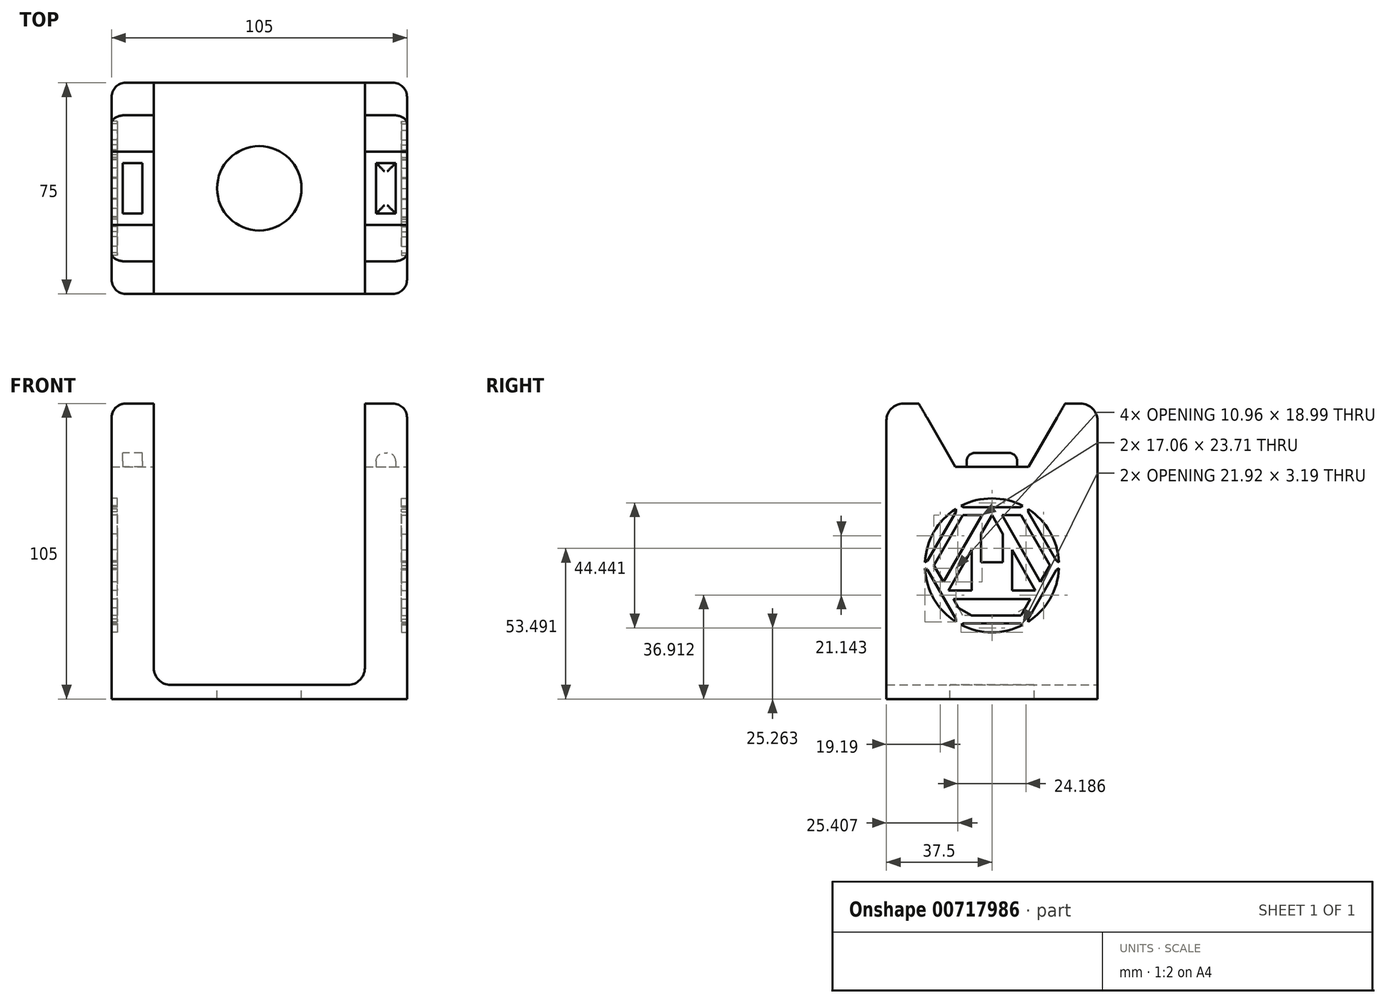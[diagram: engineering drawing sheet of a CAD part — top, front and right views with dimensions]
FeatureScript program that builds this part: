
annotation { "Feature Type Name" : "Feature", "Feature Type Description" : "" }
export const myFeature = defineFeature(function(context is Context, id is Id, definition is map)
    precondition{}
    {
        {
            var Q0;
            Q0=qCreatedBy(makeId("Front.planeOp"),FACE);
            var sketch = newSketch(context, id + "F0", { "sketchPlane" : qUnion([Q0])});
            skLineSegment(sketch, "E0.bottom", {"start": v(52.5, -2.5) * mm, "end": v(-52.5, -2.5) * mm});
            skLineSegment(sketch, "E0.top", {"start": v(52.5, 2.5) * mm, "end": v(-52.5, 2.5) * mm});
            skLineSegment(sketch, "E0.left", {"start": v(52.5, -2.5) * mm, "end": v(52.5, 2.5) * mm});
            skLineSegment(sketch, "E0.right", {"start": v(-52.5, -2.5) * mm, "end": v(-52.5, 2.5) * mm});
            skPoint(sketch, "E0.middle", {"position": v(0, 0) * mm});
            skLineSegment(sketch, "E1.bottom", {"start": v(-52.5, 2.5) * mm, "end": v(-37.5, 2.5) * mm});
            skLineSegment(sketch, "E1.top", {"start": v(-52.5, 102.5) * mm, "end": v(-37.5, 102.5) * mm});
            skLineSegment(sketch, "E1.left", {"start": v(-52.5, 2.5) * mm, "end": v(-52.5, 102.5) * mm});
            skLineSegment(sketch, "E1.right", {"start": v(-37.5, 2.5) * mm, "end": v(-37.5, 102.5) * mm});
            skLineSegment(sketch, "E2.bottom", {"start": v(52.5, 2.5) * mm, "end": v(37.5, 2.5) * mm});
            skLineSegment(sketch, "E2.top", {"start": v(52.5, 102.5) * mm, "end": v(37.5, 102.5) * mm});
            skLineSegment(sketch, "E2.left", {"start": v(52.5, 2.5) * mm, "end": v(52.5, 102.5) * mm});
            skLineSegment(sketch, "E2.right", {"start": v(37.5, 2.5) * mm, "end": v(37.5, 102.5) * mm});
            skLineSegment(sketch, "E3", {"start": v(-37.5, 2.5) * mm, "end": v(0, 2.5) * mm});
            skLineSegment(sketch, "E4", {"start": v(-37.5, 2.5) * mm, "end": v(-37.5, 40) * mm});
            skLineSegment(sketch, "E5", {"start": v(37.5, 40) * mm, "end": v(37.5, 2.5) * mm});
            skSolve(sketch);
        }
        {
            var Q0;
            Q0 = qSketchRegion(id + "F0", true);
            extrude(context, id + "F1", {"entities" : qUnion([Q0]), "depth" : 75 * mm, "offsetDistance" : 25 * mm});
        }
        {
            var Q0;
            Q0=makeQuery(id+"F1.opExtrude","SWEPT_FACE",FACE,{"disambiguationData":[OSD([sQuery(id+"F0.wireOp",EDGE,"E0.left"),sQuery(id+"F0.wireOp",EDGE,"E2.left")])]});
            var sketch = newSketch(context, id + "F2", { "sketchPlane" : qUnion([Q0])});
            skCircle(sketch, "E6.cCircle", {"center": v(-37.5, 102.5) * mm, "radius": 26 * mm, "construction": true});
            skLineSegment(sketch, "E6.0", {"start": v(-11.5, 102.5) * mm, "end": v(-24.5, 79.98) * mm});
            skLineSegment(sketch, "E6.1", {"start": v(-24.5, 79.98) * mm, "end": v(-50.5, 79.98) * mm});
            skLineSegment(sketch, "E6.2", {"start": v(-50.5, 79.98) * mm, "end": v(-63.5, 102.5) * mm});
            skLineSegment(sketch, "E6.3", {"start": v(-63.5, 102.5) * mm, "end": v(-50.5, 125.02) * mm});
            skLineSegment(sketch, "E6.4", {"start": v(-50.5, 125.02) * mm, "end": v(-24.5, 125.02) * mm});
            skLineSegment(sketch, "E6.5", {"start": v(-24.5, 125.02) * mm, "end": v(-11.5, 102.5) * mm});
            skSolve(sketch);
        }
        {
            var Q0;
            Q0 = qSketchRegion(id + "F2", true);
            extrude(context, id + "F3", {"entities" : qUnion([Q0]), "operationType" : NewBodyOperationType.REMOVE, "oppositeDirection" : true, "depth" : 122 * mm, "offsetDistance" : 25 * mm});
        }
        {
            var Q0;
            Q0=makeQuery(id+"F3.boolean.opBoolean","COPY",FACE,{"disambiguationData":[TD([makeQuery(id+"F1.opExtrude","SWEPT_FACE",FACE,{"disambiguationData":[OSD([sQuery(id+"F0.wireOp",EDGE,"E0.right"),sQuery(id+"F0.wireOp",EDGE,"E1.left")])]})])],"derivedFrom":makeQuery(id+"F3.opExtrude","SWEPT_FACE",FACE,{"disambiguationData":[OSD([sQuery(id+"F2.wireOp",EDGE,"E6.1")])]})});
            var sketch = newSketch(context, id + "F4", { "sketchPlane" : qUnion([Q0])});
            skLineSegment(sketch, "E7.bottom", {"start": v(-41.5, -50.5) * mm, "end": v(-48.5, -50.5) * mm});
            skLineSegment(sketch, "E7.top", {"start": v(-41.5, -24.5) * mm, "end": v(-48.5, -24.5) * mm});
            skLineSegment(sketch, "E7.left", {"start": v(-41.5, -50.5) * mm, "end": v(-41.5, -24.5) * mm});
            skLineSegment(sketch, "E7.right", {"start": v(-48.5, -50.5) * mm, "end": v(-48.5, -24.5) * mm});
            skPoint(sketch, "E7.middle", {"position": v(-45, -37.5) * mm});
            skPoint(sketch, "E7.middle.positionSnap0", {"position": v(-45, -24.5) * mm});
            skPoint(sketch, "E7.middle.positionSnap1", {"position": v(-37.5, -37.5) * mm});
            skPoint(sketch, "E7.centerSnap0", {"position": v(-45, -24.5) * mm});
            skPoint(sketch, "E7.centerSnap1", {"position": v(-37.5, -37.5) * mm});
            skLineSegment(sketch, "E8", {"start": v(0, 0) * mm, "end": v(0, -8.57) * mm});
            skLineSegment(sketch, "E9.MirrorCS", {"start": v(41.5, -50.5) * mm, "end": v(41.5, -24.5) * mm});
            skLineSegment(sketch, "E10.MirrorCS", {"start": v(48.5, -50.5) * mm, "end": v(48.5, -24.5) * mm});
            skLineSegment(sketch, "E11.MirrorCS", {"start": v(41.5, -24.5) * mm, "end": v(48.5, -24.5) * mm});
            skLineSegment(sketch, "E12.MirrorCS", {"start": v(41.5, -50.5) * mm, "end": v(48.5, -50.5) * mm});
            skLineSegment(sketch, "E13.bottom", {"start": v(-41.5, -46.5) * mm, "end": v(-48.5, -46.5) * mm});
            skLineSegment(sketch, "E13.top", {"start": v(-41.5, -28.5) * mm, "end": v(-48.5, -28.5) * mm});
            skLineSegment(sketch, "E13.left", {"start": v(-41.5, -46.5) * mm, "end": v(-41.5, -28.5) * mm});
            skLineSegment(sketch, "E13.right", {"start": v(-48.5, -46.5) * mm, "end": v(-48.5, -28.5) * mm});
            skLineSegment(sketch, "E14.MirrorCS", {"start": v(41.5, -28.5) * mm, "end": v(48.5, -28.5) * mm});
            skLineSegment(sketch, "E15.MirrorCS", {"start": v(41.5, -46.5) * mm, "end": v(48.5, -46.5) * mm});
            skSolve(sketch);
        }
        {
            var Q0;
            {var subQ0=sQuery(id+"F4.wireOp",EDGE,"E14.MirrorCS");Q0=makeQuery(id+"F4.imprint","IMPRINT",FACE,{"disambiguationData":[TD([[makeQuery(id+"F4.imprint","IMPRINT",EDGE,{"derivedFrom":subQ0}),-1.0]])]});}
            var Q1;
            Q1=makeQuery(id+"F4.imprint","IMPRINT",FACE,{"disambiguationData":[TD([[makeQuery(id+"F4.imprint","IMPRINT",EDGE,{"derivedFrom":sQuery(id+"F4.wireOp",EDGE,"E13.bottom")}),-1.0]])]});
            extrude(context, id + "F5", {"entities" : qUnion([Q0, Q1]), "operationType" : NewBodyOperationType.ADD, "depth" : 5 * mm, "offsetDistance" : 25 * mm});
        }
        {
            var Q0;
            Q0=makeQuery(id+"F5.opExtrude","CAP_EDGE",EDGE,{"disambiguationData":[OSD([sQuery(id+"F4.wireOp",EDGE,"E13.right")])],"isStart":false});
            var Q1;
            Q1=makeQuery(id+"F5.opExtrude","CAP_EDGE",EDGE,{"disambiguationData":[OSD([sQuery(id+"F4.wireOp",EDGE,"E13.top")])],"isStart":false});
            var Q2;
            Q2=makeQuery(id+"F5.opExtrude","CAP_EDGE",EDGE,{"disambiguationData":[OSD([sQuery(id+"F4.wireOp",EDGE,"E13.left")])],"isStart":false});
            var Q3;
            Q3=makeQuery(id+"F5.opExtrude","CAP_EDGE",EDGE,{"disambiguationData":[OSD([sQuery(id+"F4.wireOp",EDGE,"E13.bottom")])],"isStart":false});
            var Q4;
            Q4=makeQuery(id+"F5.opExtrude","CAP_EDGE",EDGE,{"disambiguationData":[OSD([sQuery(id+"F4.wireOp",EDGE,"E9.MirrorCS")])],"isStart":false});
            var Q5;
            Q5=makeQuery(id+"F5.opExtrude","CAP_EDGE",EDGE,{"disambiguationData":[OSD([sQuery(id+"F4.wireOp",EDGE,"E14.MirrorCS")])],"isStart":false});
            var Q6;
            Q6=makeQuery(id+"F5.opExtrude","CAP_EDGE",EDGE,{"disambiguationData":[OSD([sQuery(id+"F4.wireOp",EDGE,"E10.MirrorCS")])],"isStart":false});
            var Q7;
            Q7=makeQuery(id+"F5.opExtrude","CAP_EDGE",EDGE,{"disambiguationData":[OSD([sQuery(id+"F4.wireOp",EDGE,"E15.MirrorCS")])],"isStart":false});
            fillet(context, id + "F6", {"entities" : qUnion([Q0, Q1, Q2, Q3, Q4, Q5, Q6, Q7]), "radius" : 3 * mm, "tangentPropagation" : true, "allowEdgeOverflow" : false});
        }
        {
            var Q0;
            Q0=makeQuery(id+"F1.opExtrude","SWEPT_EDGE",EDGE,{"disambiguationData":[OSD([sQuery(id+"F0.wireOp",EDGE,"E1.bottom"),sQuery(id+"F0.wireOp",EDGE,"E3"),sQuery(id+"F0.wireOp",EDGE,"E4")])]});
            var Q1;
            Q1=makeQuery(id+"F1.opExtrude","SWEPT_EDGE",EDGE,{"disambiguationData":[OSD([sQuery(id+"F0.wireOp",EDGE,"E0.top"),sQuery(id+"F0.wireOp",EDGE,"E2.bottom"),sQuery(id+"F0.wireOp",EDGE,"E5")])]});
            var Q2;
            Q2=makeQuery(id+"F1.opExtrude","CAP_EDGE",EDGE,{"disambiguationData":[OSD([sQuery(id+"F0.wireOp",EDGE,"E1.top")])],"isStart":false});
            var Q3;
            Q3=makeQuery(id+"F1.opExtrude","CAP_EDGE",EDGE,{"disambiguationData":[OSD([sQuery(id+"F0.wireOp",EDGE,"E2.top")])],"isStart":false});
            var Q4;
            Q4=makeQuery(id+"F1.opExtrude","CAP_EDGE",EDGE,{"disambiguationData":[OSD([sQuery(id+"F0.wireOp",EDGE,"E2.top")])],"isStart":true});
            var Q5;
            Q5=makeQuery(id+"F1.opExtrude","CAP_EDGE",EDGE,{"disambiguationData":[OSD([sQuery(id+"F0.wireOp",EDGE,"E1.top")])],"isStart":true});
            fillet(context, id + "F7", {"entities" : qUnion([Q0, Q1, Q2, Q3, Q4, Q5]), "radius" : 6 * mm, "tangentPropagation" : true, "allowEdgeOverflow" : false});
        }
        {
            var Q0;
            Q0=makeQuery(id+"F1.opExtrude","CAP_EDGE",EDGE,{"disambiguationData":[OSD([sQuery(id+"F0.wireOp",EDGE,"E0.right"),sQuery(id+"F0.wireOp",EDGE,"E1.left")])],"isStart":false});
            var Q1;
            Q1=makeQuery(id+"F1.opExtrude","CAP_EDGE",EDGE,{"disambiguationData":[OSD([sQuery(id+"F0.wireOp",EDGE,"E0.right"),sQuery(id+"F0.wireOp",EDGE,"E1.left")])],"isStart":true});
            var Q2;
            Q2=makeQuery(id+"F1.opExtrude","CAP_EDGE",EDGE,{"disambiguationData":[OSD([sQuery(id+"F0.wireOp",EDGE,"E0.left"),sQuery(id+"F0.wireOp",EDGE,"E2.left")])],"isStart":false});
            var Q3;
            Q3=makeQuery(id+"F1.opExtrude","CAP_EDGE",EDGE,{"disambiguationData":[OSD([sQuery(id+"F0.wireOp",EDGE,"E0.left"),sQuery(id+"F0.wireOp",EDGE,"E2.left")])],"isStart":true});
            fillet(context, id + "F8", {"entities" : qUnion([Q0, Q1, Q2, Q3]), "radius" : 5 * mm, "tangentPropagation" : true, "allowEdgeOverflow" : false});
        }
        {
            var Q0;
            Q0=makeQuery(id+"F1.opExtrude","SWEPT_FACE",FACE,{"disambiguationData":[OSD([sQuery(id+"F0.wireOp",EDGE,"E0.left"),sQuery(id+"F0.wireOp",EDGE,"E2.left")])]});
            var sketch = newSketch(context, id + "F9", { "sketchPlane" : qUnion([Q0])});
            skCircle(sketch, "E16", {"center": v(-37.5, 44.98) * mm, "radius": 27.5 * mm});
            skLineSegment(sketch, "E17", {"start": v(-51.25, 68.8) * mm, "end": v(-65, 44.98) * mm});
            skLineSegment(sketch, "E18", {"start": v(-65, 44.98) * mm, "end": v(-51.25, 21.17) * mm});
            skLineSegment(sketch, "E19", {"start": v(-51.25, 21.17) * mm, "end": v(-23.75, 21.17) * mm});
            skLineSegment(sketch, "E20", {"start": v(-23.75, 21.17) * mm, "end": v(-10, 44.98) * mm});
            skLineSegment(sketch, "E21", {"start": v(-10, 44.98) * mm, "end": v(-23.75, 68.8) * mm});
            skLineSegment(sketch, "E22", {"start": v(-23.75, 68.8) * mm, "end": v(-51.25, 68.8) * mm});
            skCircle(sketch, "E23", {"center": v(-37.5, 44.98) * mm, "radius": 23.82 * mm});
            skLineSegment(sketch, "E24", {"start": v(-49.4, 65.6) * mm, "end": v(-61.32, 44.98) * mm});
            skLineSegment(sketch, "E25", {"start": v(-61.32, 44.98) * mm, "end": v(-49.4, 24.36) * mm});
            skLineSegment(sketch, "E26", {"start": v(-49.4, 24.36) * mm, "end": v(-25.6, 24.36) * mm});
            skLineSegment(sketch, "E27", {"start": v(-25.6, 24.36) * mm, "end": v(-13.68, 44.98) * mm});
            skLineSegment(sketch, "E28", {"start": v(-13.68, 44.98) * mm, "end": v(-25.6, 65.6) * mm});
            skLineSegment(sketch, "E29", {"start": v(-25.6, 65.6) * mm, "end": v(-49.4, 65.6) * mm});
            skLineSegment(sketch, "E30", {"start": v(-51.25, 27.55) * mm, "end": v(-51.25, 25.54) * mm});
            skLineSegment(sketch, "E31", {"start": v(-23.75, 27.55) * mm, "end": v(-23.75, 25.54) * mm});
            skLineSegment(sketch, "E32", {"start": v(-49.4, 24.36) * mm, "end": v(-51.25, 21.17) * mm});
            skLineSegment(sketch, "E33", {"start": v(-25.6, 24.36) * mm, "end": v(-23.75, 21.17) * mm});
            skLineSegment(sketch, "E34.MirrorCS", {"start": v(-45.72, 24.36) * mm, "end": v(-47.47, 23.35) * mm});
            skLineSegment(sketch, "E35.MirrorCS", {"start": v(-29.28, 24.36) * mm, "end": v(-27.53, 23.35) * mm});
            skLineSegment(sketch, "E36", {"start": v(-37.5, 44.98) * mm, "end": v(-37.6, 44.98) * mm});
            skLineSegment(sketch, "E37.MirrorCS", {"start": v(-51.25, 62.42) * mm, "end": v(-51.25, 64.43) * mm});
            skLineSegment(sketch, "E38.MirrorCS", {"start": v(-45.72, 65.6) * mm, "end": v(-47.47, 66.61) * mm});
            skLineSegment(sketch, "E39.MirrorCS", {"start": v(-29.28, 65.6) * mm, "end": v(-27.53, 66.61) * mm});
            skLineSegment(sketch, "E40.MirrorCS", {"start": v(-23.75, 62.42) * mm, "end": v(-23.75, 64.43) * mm});
            skLineSegment(sketch, "E41", {"start": v(-58.12, 33.08) * mm, "end": v(-55.36, 34.67) * mm});
            skLineSegment(sketch, "E42", {"start": v(-19.64, 34.67) * mm, "end": v(-16.87, 33.08) * mm});
            skLineSegment(sketch, "E43.MirrorCS", {"start": v(-59.47, 41.8) * mm, "end": v(-61.22, 42.8) * mm});
            skLineSegment(sketch, "E44.MirrorCS", {"start": v(-59.47, 48.17) * mm, "end": v(-61.22, 47.17) * mm});
            skLineSegment(sketch, "E45.MirrorCS", {"start": v(-15.53, 48.17) * mm, "end": v(-13.78, 47.17) * mm});
            skLineSegment(sketch, "E46.MirrorCS", {"start": v(-15.53, 41.8) * mm, "end": v(-13.78, 42.8) * mm});
            skCircle(sketch, "E47", {"center": v(-37.5, 44.98) * mm, "radius": 20.63 * mm});
            skLineSegment(sketch, "E48", {"start": v(-47.81, 62.85) * mm, "end": v(-58.13, 44.98) * mm});
            skLineSegment(sketch, "E49", {"start": v(-58.13, 44.98) * mm, "end": v(-47.81, 27.12) * mm});
            skLineSegment(sketch, "E50", {"start": v(-47.81, 27.12) * mm, "end": v(-27.19, 27.12) * mm});
            skLineSegment(sketch, "E51", {"start": v(-27.19, 27.12) * mm, "end": v(-16.87, 44.98) * mm});
            skLineSegment(sketch, "E52", {"start": v(-16.87, 44.98) * mm, "end": v(-27.19, 62.85) * mm});
            skLineSegment(sketch, "E53", {"start": v(-27.19, 62.85) * mm, "end": v(-47.81, 62.85) * mm});
            skLineSegment(sketch, "E54", {"start": v(-44.62, 27.12) * mm, "end": v(-47.81, 27.12) * mm});
            skLineSegment(sketch, "E55", {"start": v(-47.81, 27.12) * mm, "end": v(-49.4, 29.88) * mm});
            skLineSegment(sketch, "E56", {"start": v(-49.4, 29.88) * mm, "end": v(-44.62, 27.12) * mm});
            skLineSegment(sketch, "E57", {"start": v(-37.5, 27.12) * mm, "end": v(-37.5, 24.36) * mm});
            skLineSegment(sketch, "E58", {"start": v(-55.36, 34.67) * mm, "end": v(-52.97, 36.05) * mm});
            skLineSegment(sketch, "E59.MirrorCS", {"start": v(-25.6, 29.88) * mm, "end": v(-30.38, 27.12) * mm});
            skLineSegment(sketch, "E60.MirrorCS", {"start": v(-49.4, 60.08) * mm, "end": v(-44.62, 62.85) * mm});
            skLineSegment(sketch, "E61.MirrorCS", {"start": v(-25.6, 60.08) * mm, "end": v(-30.38, 62.85) * mm});
            skLineSegment(sketch, "E62.MirrorCS", {"start": v(-56.53, 42.22) * mm, "end": v(-56.53, 47.75) * mm});
            skLineSegment(sketch, "E63", {"start": v(-37.5, 44.98) * mm, "end": v(-37.5, 45.08) * mm});
            skLineSegment(sketch, "E64.MirrorCS", {"start": v(-18.47, 42.22) * mm, "end": v(-18.47, 47.75) * mm});
            skLineSegment(sketch, "E65", {"start": v(-52.97, 36.05) * mm, "end": v(-22.03, 36.05) * mm});
            skLineSegment(sketch, "E66", {"start": v(-22.03, 36.05) * mm, "end": v(-37.5, 62.85) * mm});
            skLineSegment(sketch, "E67", {"start": v(-37.5, 62.85) * mm, "end": v(-52.97, 36.05) * mm});
            skLineSegment(sketch, "E68", {"start": v(-44.62, 62.85) * mm, "end": v(-37.5, 62.85) * mm});
            skLineSegment(sketch, "E69", {"start": v(-41.06, 62.85) * mm, "end": v(-54.75, 39.14) * mm});
            skLineSegment(sketch, "E70", {"start": v(-37.5, 62.85) * mm, "end": v(-30.38, 62.85) * mm});
            skLineSegment(sketch, "E71", {"start": v(-33.94, 62.85) * mm, "end": v(-20.25, 39.14) * mm});
            skLineSegment(sketch, "E72", {"start": v(-52.97, 36.05) * mm, "end": v(-49.4, 29.88) * mm});
            skLineSegment(sketch, "E73", {"start": v(-51.19, 32.97) * mm, "end": v(-23.81, 32.97) * mm});
            skLineSegment(sketch, "E74", {"start": v(-51.25, 27.55) * mm, "end": v(-49.4, 24.36) * mm});
            skLineSegment(sketch, "E75", {"start": v(-50.33, 25.95) * mm, "end": v(-50.33, 24.92) * mm});
            skPoint(sketch, "E75.endSnap0", {"position": v(-50.33, 25.95) * mm});
            skLineSegment(sketch, "E76.MirrorCS", {"start": v(-47.57, 24.36) * mm, "end": v(-48.46, 23.84) * mm});
            skLineSegment(sketch, "E77.MirrorCS", {"start": v(-24.67, 25.95) * mm, "end": v(-24.67, 24.92) * mm});
            skLineSegment(sketch, "E78.MirrorCS", {"start": v(-27.43, 24.36) * mm, "end": v(-26.54, 23.84) * mm});
            skLineSegment(sketch, "E79.MirrorCS", {"start": v(-47.57, 65.6) * mm, "end": v(-48.46, 66.13) * mm});
            skLineSegment(sketch, "E80.MirrorCS", {"start": v(-50.33, 64.01) * mm, "end": v(-50.33, 65.05) * mm});
            skLineSegment(sketch, "E81.MirrorCS", {"start": v(-27.43, 65.6) * mm, "end": v(-26.54, 66.13) * mm});
            skLineSegment(sketch, "E82.MirrorCS", {"start": v(-24.67, 64.01) * mm, "end": v(-24.67, 65.05) * mm});
            skLineSegment(sketch, "E83.MirrorCS", {"start": v(-60.4, 43.39) * mm, "end": v(-61.3, 43.9) * mm});
            skLineSegment(sketch, "E84.MirrorCS", {"start": v(-60.4, 46.58) * mm, "end": v(-61.3, 46.06) * mm});
            skLineSegment(sketch, "E85.MirrorCS", {"start": v(-14.6, 46.58) * mm, "end": v(-13.7, 46.06) * mm});
            skLineSegment(sketch, "E86.MirrorCS", {"start": v(-14.6, 43.39) * mm, "end": v(-13.7, 43.9) * mm});
            skLineSegment(sketch, "E87", {"start": v(-45.23, 49.45) * mm, "end": v(-37.5, 62.85) * mm});
            skLineSegment(sketch, "E88", {"start": v(-37.5, 62.85) * mm, "end": v(-29.77, 49.45) * mm});
            skLineSegment(sketch, "E89", {"start": v(-41.37, 56.15) * mm, "end": v(-41.37, 36.05) * mm});
            skLineSegment(sketch, "E90", {"start": v(-41.37, 36.05) * mm, "end": v(-44.62, 36.05) * mm});
            skLineSegment(sketch, "E91", {"start": v(-44.62, 36.05) * mm, "end": v(-44.62, 50.5) * mm});
            skLineSegment(sketch, "E92", {"start": v(-41.37, 44.98) * mm, "end": v(-37.5, 44.98) * mm});
            skLineSegment(sketch, "E93", {"start": v(-41.37, 36.05) * mm, "end": v(-41.37, 44.98) * mm});
            skLineSegment(sketch, "E94", {"start": v(-41.37, 40.52) * mm, "end": v(-41.37, 44.98) * mm});
            skLineSegment(sketch, "E95", {"start": v(-41.37, 42.75) * mm, "end": v(-41.37, 44.98) * mm});
            skLineSegment(sketch, "E96", {"start": v(-41.37, 43.87) * mm, "end": v(-37.5, 43.87) * mm});
            skLineSegment(sketch, "E97", {"start": v(-30.38, 50.5) * mm, "end": v(-30.38, 36.05) * mm});
            skLineSegment(sketch, "E98", {"start": v(-33.63, 56.15) * mm, "end": v(-33.63, 36.05) * mm});
            skLineSegment(sketch, "E99", {"start": v(-37.6, 44.98) * mm, "end": v(-41.37, 44.98) * mm});
            skLineSegment(sketch, "E100", {"start": v(-37.5, 43.87) * mm, "end": v(-33.63, 43.87) * mm});
            skLineSegment(sketch, "E101", {"start": v(-37.5, 44.98) * mm, "end": v(-33.63, 44.98) * mm});
            skLineSegment(sketch, "E102", {"start": v(-33.63, 36.05) * mm, "end": v(-33.63, 44.98) * mm});
            skLineSegment(sketch, "E103", {"start": v(-33.63, 36.05) * mm, "end": v(-33.63, 43.87) * mm});
            skLineSegment(sketch, "E104", {"start": v(-33.63, 44.98) * mm, "end": v(-33.63, 43.87) * mm});
            skLineSegment(sketch, "E105.MirrorCS", {"start": v(-37.5, 46.1) * mm, "end": v(-33.63, 46.1) * mm});
            skLineSegment(sketch, "E106.MirrorCS", {"start": v(-41.37, 46.1) * mm, "end": v(-37.5, 46.1) * mm});
            skLineSegment(sketch, "E107", {"start": v(-37.5, 44.98) * mm, "end": v(-37.5, 79.98) * mm});
            skSolve(sketch);
        }
        {
            var Q0;
            {var subQ3=sQuery(id+"F9.wireOp",EDGE,"E60.MirrorCS");Q0=makeQuery(id+"F9.imprint","IMPRINT",FACE,{"disambiguationData":[TD([[makeQuery(id+"F9.imprint","IMPRINT",EDGE,{"derivedFrom":subQ3}),-1.0]])]});}
            var Q1;
            {var subQ3=sQuery(id+"F9.wireOp",EDGE,"E56");Q1=makeQuery(id+"F9.imprint","IMPRINT",FACE,{"disambiguationData":[TD([[makeQuery(id+"F9.imprint","IMPRINT",EDGE,{"derivedFrom":subQ3}),1.0]])]});}
            var Q2;
            {var subQ0=sQuery(id+"F9.wireOp",EDGE,"E66");Q2=makeQuery(id+"F9.imprint","IMPRINT",FACE,{"disambiguationData":[TD([[makeQuery(id+"F9.imprint","IMPRINT",EDGE,{"derivedFrom":subQ0}),1.0]])]});}
            var Q3;
            {var subQ2=sQuery(id+"F9.wireOp",EDGE,"E61.MirrorCS");Q3=makeQuery(id+"F9.imprint","IMPRINT",FACE,{"disambiguationData":[TD([[makeQuery(id+"F9.imprint","IMPRINT",EDGE,{"derivedFrom":subQ2}),1.0]])]});}
            var Q4;
            {var subQ0=sQuery(id+"F9.wireOp",EDGE,"E67");Q4=makeQuery(id+"F9.imprint","IMPRINT",FACE,{"disambiguationData":[TD([[makeQuery(id+"F9.imprint","IMPRINT",EDGE,{"derivedFrom":subQ0}),1.0]])]});}
            var Q5;
            {var subQ3=sQuery(id+"F9.wireOp",EDGE,"E93");Q5=makeQuery(id+"F9.imprint","IMPRINT",FACE,{"disambiguationData":[TD([[makeQuery(id+"F9.imprint","IMPRINT",EDGE,{"derivedFrom":subQ3}),-1.0]])]});}
            var Q6;
            {var subQ5=sQuery(id+"F9.wireOp",EDGE,"E106.MirrorCS");Q6=makeQuery(id+"F9.imprint","IMPRINT",FACE,{"disambiguationData":[TD([[makeQuery(id+"F9.imprint","IMPRINT",EDGE,{"derivedFrom":subQ5}),1.0]])]});}
            var Q7;
            {var subQ5=sQuery(id+"F9.wireOp",EDGE,"E105.MirrorCS");Q7=makeQuery(id+"F9.imprint","IMPRINT",FACE,{"disambiguationData":[TD([[makeQuery(id+"F9.imprint","IMPRINT",EDGE,{"derivedFrom":subQ5}),1.0]])]});}
            var Q8;
            {var subQ0=sQuery(id+"F9.wireOp",EDGE,"E30");Q8=makeQuery(id+"F9.imprint","IMPRINT",FACE,{"disambiguationData":[TD([[makeQuery(id+"F9.imprint","IMPRINT",EDGE,{"derivedFrom":subQ0}),-1.0]])]});}
            var Q9;
            {var subQ0=sQuery(id+"F9.wireOp",EDGE,"E41");Q9=makeQuery(id+"F9.imprint","IMPRINT",FACE,{"disambiguationData":[TD([[makeQuery(id+"F9.imprint","IMPRINT",EDGE,{"derivedFrom":subQ0}),1.0]])]});}
            var Q10;
            {var subQ0=sQuery(id+"F9.wireOp",EDGE,"E43.MirrorCS");Q10=makeQuery(id+"F9.imprint","IMPRINT",FACE,{"disambiguationData":[TD([[makeQuery(id+"F9.imprint","IMPRINT",EDGE,{"derivedFrom":subQ0}),-1.0]])]});}
            var Q11;
            {var subQ0=sQuery(id+"F9.wireOp",EDGE,"E44.MirrorCS");Q11=makeQuery(id+"F9.imprint","IMPRINT",FACE,{"disambiguationData":[TD([[makeQuery(id+"F9.imprint","IMPRINT",EDGE,{"derivedFrom":subQ0}),1.0]])]});}
            var Q12;
            {var subQ0=sQuery(id+"F9.wireOp",EDGE,"E37.MirrorCS");Q12=makeQuery(id+"F9.imprint","IMPRINT",FACE,{"disambiguationData":[TD([[makeQuery(id+"F9.imprint","IMPRINT",EDGE,{"derivedFrom":subQ0}),1.0]])]});}
            var Q13;
            {var subQ0=sQuery(id+"F9.wireOp",EDGE,"E30");Q13=makeQuery(id+"F9.imprint","IMPRINT",FACE,{"disambiguationData":[TD([[makeQuery(id+"F9.imprint","IMPRINT",EDGE,{"derivedFrom":subQ0}),1.0]])]});}
            var Q14;
            {var subQ0=sQuery(id+"F9.wireOp",EDGE,"E34.MirrorCS");Q14=makeQuery(id+"F9.imprint","IMPRINT",FACE,{"disambiguationData":[TD([[makeQuery(id+"F9.imprint","IMPRINT",EDGE,{"derivedFrom":subQ0}),-1.0]])]});}
            var Q15;
            {var subQ5=sQuery(id+"F9.wireOp",EDGE,"E34.MirrorCS");Q15=makeQuery(id+"F9.imprint","IMPRINT",FACE,{"disambiguationData":[TD([[makeQuery(id+"F9.imprint","IMPRINT",EDGE,{"derivedFrom":subQ5}),1.0]])]});}
            var Q16;
            {var subQ0=sQuery(id+"F9.wireOp",EDGE,"E35.MirrorCS");Q16=makeQuery(id+"F9.imprint","IMPRINT",FACE,{"disambiguationData":[TD([[makeQuery(id+"F9.imprint","IMPRINT",EDGE,{"derivedFrom":subQ0}),1.0]])]});}
            var Q17;
            {var subQ0=sQuery(id+"F9.wireOp",EDGE,"E31");Q17=makeQuery(id+"F9.imprint","IMPRINT",FACE,{"disambiguationData":[TD([[makeQuery(id+"F9.imprint","IMPRINT",EDGE,{"derivedFrom":subQ0}),1.0]])]});}
            var Q18;
            {var subQ0=sQuery(id+"F9.wireOp",EDGE,"E31");Q18=makeQuery(id+"F9.imprint","IMPRINT",FACE,{"disambiguationData":[TD([[makeQuery(id+"F9.imprint","IMPRINT",EDGE,{"derivedFrom":subQ0}),-1.0]])]});}
            var Q19;
            {var subQ0=sQuery(id+"F9.wireOp",EDGE,"E42");Q19=makeQuery(id+"F9.imprint","IMPRINT",FACE,{"disambiguationData":[TD([[makeQuery(id+"F9.imprint","IMPRINT",EDGE,{"derivedFrom":subQ0}),1.0]])]});}
            var Q20;
            {var subQ0=sQuery(id+"F9.wireOp",EDGE,"E46.MirrorCS");Q20=makeQuery(id+"F9.imprint","IMPRINT",FACE,{"disambiguationData":[TD([[makeQuery(id+"F9.imprint","IMPRINT",EDGE,{"derivedFrom":subQ0}),1.0]])]});}
            var Q21;
            {var subQ0=sQuery(id+"F9.wireOp",EDGE,"E45.MirrorCS");Q21=makeQuery(id+"F9.imprint","IMPRINT",FACE,{"disambiguationData":[TD([[makeQuery(id+"F9.imprint","IMPRINT",EDGE,{"derivedFrom":subQ0}),-1.0]])]});}
            var Q22;
            {var subQ0=sQuery(id+"F9.wireOp",EDGE,"E40.MirrorCS");Q22=makeQuery(id+"F9.imprint","IMPRINT",FACE,{"disambiguationData":[TD([[makeQuery(id+"F9.imprint","IMPRINT",EDGE,{"derivedFrom":subQ0}),-1.0]])]});}
            var Q23;
            {var subQ0=sQuery(id+"F9.wireOp",EDGE,"E40.MirrorCS");Q23=makeQuery(id+"F9.imprint","IMPRINT",FACE,{"disambiguationData":[TD([[makeQuery(id+"F9.imprint","IMPRINT",EDGE,{"derivedFrom":subQ0}),1.0]])]});}
            var Q24;
            {var subQ0=sQuery(id+"F9.wireOp",EDGE,"E39.MirrorCS");Q24=makeQuery(id+"F9.imprint","IMPRINT",FACE,{"disambiguationData":[TD([[makeQuery(id+"F9.imprint","IMPRINT",EDGE,{"derivedFrom":subQ0}),-1.0]])]});}
            var Q25;
            {var subQ0=sQuery(id+"F9.wireOp",EDGE,"E39.MirrorCS");Q25=makeQuery(id+"F9.imprint","IMPRINT",FACE,{"disambiguationData":[TD([[makeQuery(id+"F9.imprint","IMPRINT",EDGE,{"derivedFrom":subQ0}),1.0]])]});}
            var Q26;
            {var subQ0=sQuery(id+"F9.wireOp",EDGE,"E38.MirrorCS");Q26=makeQuery(id+"F9.imprint","IMPRINT",FACE,{"disambiguationData":[TD([[makeQuery(id+"F9.imprint","IMPRINT",EDGE,{"derivedFrom":subQ0}),-1.0]])]});}
            var Q27;
            {var subQ0=sQuery(id+"F9.wireOp",EDGE,"E38.MirrorCS");Q27=makeQuery(id+"F9.imprint","IMPRINT",FACE,{"disambiguationData":[TD([[makeQuery(id+"F9.imprint","IMPRINT",EDGE,{"derivedFrom":subQ0}),1.0]])]});}
            var Q28;
            {var subQ0=sQuery(id+"F9.wireOp",EDGE,"E37.MirrorCS");Q28=makeQuery(id+"F9.imprint","IMPRINT",FACE,{"disambiguationData":[TD([[makeQuery(id+"F9.imprint","IMPRINT",EDGE,{"derivedFrom":subQ0}),-1.0]])]});}
            var Q29;
            {var subQ3=sQuery(id+"F9.wireOp",EDGE,"E60.MirrorCS");Q29=makeQuery(id+"F9.imprint","IMPRINT",FACE,{"disambiguationData":[TD([[makeQuery(id+"F9.imprint","IMPRINT",EDGE,{"derivedFrom":subQ3}),1.0]])]});}
            var Q30;
            {var subQ3=sQuery(id+"F9.wireOp",EDGE,"E61.MirrorCS");Q30=makeQuery(id+"F9.imprint","IMPRINT",FACE,{"disambiguationData":[TD([[makeQuery(id+"F9.imprint","IMPRINT",EDGE,{"derivedFrom":subQ3}),-1.0]])]});}
            var Q31;
            {var subQ3=sQuery(id+"F9.wireOp",EDGE,"E64.MirrorCS");Q31=makeQuery(id+"F9.imprint","IMPRINT",FACE,{"disambiguationData":[TD([[makeQuery(id+"F9.imprint","IMPRINT",EDGE,{"derivedFrom":subQ3}),-1.0]])]});}
            var Q32;
            {var subQ3=sQuery(id+"F9.wireOp",EDGE,"E59.MirrorCS");Q32=makeQuery(id+"F9.imprint","IMPRINT",FACE,{"disambiguationData":[TD([[makeQuery(id+"F9.imprint","IMPRINT",EDGE,{"derivedFrom":subQ3}),1.0]])]});}
            var Q33;
            Q33=makeQuery(id+"F9.imprint","IMPRINT",FACE,{"disambiguationData":[TD([[makeQuery(id+"F9.imprint","IMPRINT",EDGE,{"derivedFrom":sQuery(id+"F9.wireOp",EDGE,"E55")}),-1.0]])]});
            var Q34;
            {var subQ3=sQuery(id+"F9.wireOp",EDGE,"E62.MirrorCS");Q34=makeQuery(id+"F9.imprint","IMPRINT",FACE,{"disambiguationData":[TD([[makeQuery(id+"F9.imprint","IMPRINT",EDGE,{"derivedFrom":subQ3}),1.0]])]});}
            extrude(context, id + "F10", {"entities" : qUnion([Q0, Q1, Q2, Q3, Q4, Q5, Q6, Q7, Q8, Q9, Q10, Q11, Q12, Q13, Q14, Q15, Q16, Q17, Q18, Q19, Q20, Q21, Q22, Q23, Q24, Q25, Q26, Q27, Q28, Q29, Q30, Q31, Q32, Q33, Q34]), "operationType" : NewBodyOperationType.REMOVE, "oppositeDirection" : true, "depth" : 2 * mm, "offsetDistance" : 25 * mm});
        }
        {
            var Q0;
            Q0=makeQuery(id+"F1.opExtrude","SWEPT_FACE",FACE,{"disambiguationData":[OSD([sQuery(id+"F0.wireOp",EDGE,"E0.right"),sQuery(id+"F0.wireOp",EDGE,"E1.left")])]});
            var sketch = newSketch(context, id + "F11", { "sketchPlane" : qUnion([Q0])});
            skCircle(sketch, "E108", {"center": v(37.5, 44.98) * mm, "radius": 27.5 * mm});
            skLineSegment(sketch, "E109", {"start": v(23.75, 68.8) * mm, "end": v(10, 44.98) * mm});
            skLineSegment(sketch, "E110", {"start": v(10, 44.98) * mm, "end": v(23.75, 21.17) * mm});
            skLineSegment(sketch, "E111", {"start": v(23.75, 21.17) * mm, "end": v(51.25, 21.17) * mm});
            skLineSegment(sketch, "E112", {"start": v(51.25, 21.17) * mm, "end": v(65, 44.98) * mm});
            skLineSegment(sketch, "E113", {"start": v(65, 44.98) * mm, "end": v(51.25, 68.8) * mm});
            skLineSegment(sketch, "E114", {"start": v(51.25, 68.8) * mm, "end": v(23.75, 68.8) * mm});
            skCircle(sketch, "E115", {"center": v(37.5, 44.98) * mm, "radius": 23.82 * mm});
            skLineSegment(sketch, "E116", {"start": v(25.6, 65.6) * mm, "end": v(13.68, 44.98) * mm});
            skLineSegment(sketch, "E117", {"start": v(13.68, 44.98) * mm, "end": v(25.6, 24.36) * mm});
            skLineSegment(sketch, "E118", {"start": v(25.6, 24.36) * mm, "end": v(49.4, 24.36) * mm});
            skLineSegment(sketch, "E119", {"start": v(49.4, 24.36) * mm, "end": v(61.32, 44.98) * mm});
            skLineSegment(sketch, "E120", {"start": v(61.32, 44.98) * mm, "end": v(49.4, 65.6) * mm});
            skLineSegment(sketch, "E121", {"start": v(49.4, 65.6) * mm, "end": v(25.6, 65.6) * mm});
            skLineSegment(sketch, "E122", {"start": v(23.75, 27.55) * mm, "end": v(23.75, 25.54) * mm});
            skLineSegment(sketch, "E123", {"start": v(51.25, 27.55) * mm, "end": v(51.25, 25.54) * mm});
            skLineSegment(sketch, "E124", {"start": v(25.6, 24.36) * mm, "end": v(23.75, 21.17) * mm});
            skLineSegment(sketch, "E125", {"start": v(49.4, 24.36) * mm, "end": v(51.25, 21.17) * mm});
            skLineSegment(sketch, "E126.MirrorCS", {"start": v(29.28, 24.36) * mm, "end": v(27.53, 23.35) * mm});
            skLineSegment(sketch, "E127.MirrorCS", {"start": v(45.72, 24.36) * mm, "end": v(47.47, 23.35) * mm});
            skLineSegment(sketch, "E128", {"start": v(37.5, 44.98) * mm, "end": v(37.4, 44.98) * mm});
            skLineSegment(sketch, "E129.MirrorCS", {"start": v(23.75, 62.42) * mm, "end": v(23.75, 64.43) * mm});
            skLineSegment(sketch, "E130.MirrorCS", {"start": v(29.28, 65.6) * mm, "end": v(27.53, 66.61) * mm});
            skLineSegment(sketch, "E131.MirrorCS", {"start": v(45.72, 65.6) * mm, "end": v(47.47, 66.61) * mm});
            skLineSegment(sketch, "E132.MirrorCS", {"start": v(51.25, 62.42) * mm, "end": v(51.25, 64.43) * mm});
            skLineSegment(sketch, "E133", {"start": v(16.88, 33.08) * mm, "end": v(19.64, 34.67) * mm});
            skLineSegment(sketch, "E134", {"start": v(55.36, 34.67) * mm, "end": v(58.12, 33.08) * mm});
            skLineSegment(sketch, "E135.MirrorCS", {"start": v(15.53, 41.8) * mm, "end": v(13.78, 42.8) * mm});
            skLineSegment(sketch, "E136.MirrorCS", {"start": v(15.53, 48.17) * mm, "end": v(13.78, 47.17) * mm});
            skLineSegment(sketch, "E137.MirrorCS", {"start": v(59.47, 48.17) * mm, "end": v(61.22, 47.17) * mm});
            skLineSegment(sketch, "E138.MirrorCS", {"start": v(59.47, 41.8) * mm, "end": v(61.22, 42.8) * mm});
            skCircle(sketch, "E139", {"center": v(37.5, 44.98) * mm, "radius": 20.62 * mm});
            skLineSegment(sketch, "E140", {"start": v(27.19, 62.85) * mm, "end": v(16.88, 44.98) * mm});
            skLineSegment(sketch, "E141", {"start": v(16.88, 44.98) * mm, "end": v(27.19, 27.12) * mm});
            skLineSegment(sketch, "E142", {"start": v(27.19, 27.12) * mm, "end": v(47.81, 27.12) * mm});
            skLineSegment(sketch, "E143", {"start": v(47.81, 27.12) * mm, "end": v(58.12, 44.98) * mm});
            skLineSegment(sketch, "E144", {"start": v(58.12, 44.98) * mm, "end": v(47.81, 62.85) * mm});
            skLineSegment(sketch, "E145", {"start": v(47.81, 62.85) * mm, "end": v(27.19, 62.85) * mm});
            skLineSegment(sketch, "E146", {"start": v(30.38, 27.12) * mm, "end": v(27.19, 27.12) * mm});
            skLineSegment(sketch, "E147", {"start": v(27.19, 27.12) * mm, "end": v(25.6, 29.88) * mm});
            skLineSegment(sketch, "E148", {"start": v(25.6, 29.88) * mm, "end": v(30.38, 27.12) * mm});
            skLineSegment(sketch, "E149", {"start": v(37.5, 27.12) * mm, "end": v(37.5, 24.36) * mm});
            skLineSegment(sketch, "E150", {"start": v(19.64, 34.67) * mm, "end": v(22.03, 36.05) * mm});
            skLineSegment(sketch, "E151.MirrorCS", {"start": v(49.4, 29.88) * mm, "end": v(44.62, 27.12) * mm});
            skLineSegment(sketch, "E152.MirrorCS", {"start": v(25.6, 60.08) * mm, "end": v(30.38, 62.85) * mm});
            skLineSegment(sketch, "E153.MirrorCS", {"start": v(49.4, 60.08) * mm, "end": v(44.62, 62.85) * mm});
            skLineSegment(sketch, "E154.MirrorCS", {"start": v(18.47, 42.22) * mm, "end": v(18.47, 47.75) * mm});
            skLineSegment(sketch, "E155", {"start": v(37.5, 44.98) * mm, "end": v(37.5, 45.08) * mm});
            skLineSegment(sketch, "E156.MirrorCS", {"start": v(56.53, 42.22) * mm, "end": v(56.53, 47.75) * mm});
            skLineSegment(sketch, "E157", {"start": v(22.03, 36.05) * mm, "end": v(52.97, 36.05) * mm});
            skLineSegment(sketch, "E158", {"start": v(52.97, 36.05) * mm, "end": v(37.5, 62.85) * mm});
            skLineSegment(sketch, "E159", {"start": v(37.5, 62.85) * mm, "end": v(22.03, 36.05) * mm});
            skLineSegment(sketch, "E160", {"start": v(30.38, 62.85) * mm, "end": v(37.5, 62.85) * mm});
            skLineSegment(sketch, "E161", {"start": v(33.94, 62.85) * mm, "end": v(20.25, 39.14) * mm});
            skLineSegment(sketch, "E162", {"start": v(37.5, 62.85) * mm, "end": v(44.62, 62.85) * mm});
            skLineSegment(sketch, "E163", {"start": v(41.06, 62.85) * mm, "end": v(54.75, 39.14) * mm});
            skLineSegment(sketch, "E164", {"start": v(22.03, 36.05) * mm, "end": v(25.6, 29.88) * mm});
            skLineSegment(sketch, "E165", {"start": v(23.81, 32.97) * mm, "end": v(51.19, 32.97) * mm});
            skLineSegment(sketch, "E166", {"start": v(23.75, 27.55) * mm, "end": v(25.6, 24.36) * mm});
            skLineSegment(sketch, "E167", {"start": v(24.67, 25.95) * mm, "end": v(24.67, 24.92) * mm});
            skPoint(sketch, "E167.endSnap0", {"position": v(24.67, 25.95) * mm});
            skLineSegment(sketch, "E168.MirrorCS", {"start": v(27.43, 24.36) * mm, "end": v(26.54, 23.84) * mm});
            skLineSegment(sketch, "E169.MirrorCS", {"start": v(50.33, 25.95) * mm, "end": v(50.33, 24.92) * mm});
            skLineSegment(sketch, "E170.MirrorCS", {"start": v(47.57, 24.36) * mm, "end": v(48.46, 23.84) * mm});
            skLineSegment(sketch, "E171.MirrorCS", {"start": v(27.43, 65.6) * mm, "end": v(26.54, 66.13) * mm});
            skLineSegment(sketch, "E172.MirrorCS", {"start": v(24.67, 64.01) * mm, "end": v(24.67, 65.05) * mm});
            skLineSegment(sketch, "E173.MirrorCS", {"start": v(47.57, 65.6) * mm, "end": v(48.46, 66.13) * mm});
            skLineSegment(sketch, "E174.MirrorCS", {"start": v(50.33, 64.01) * mm, "end": v(50.33, 65.05) * mm});
            skLineSegment(sketch, "E175.MirrorCS", {"start": v(14.6, 43.39) * mm, "end": v(13.7, 43.9) * mm});
            skLineSegment(sketch, "E176.MirrorCS", {"start": v(14.6, 46.58) * mm, "end": v(13.7, 46.06) * mm});
            skLineSegment(sketch, "E177.MirrorCS", {"start": v(60.4, 46.58) * mm, "end": v(61.3, 46.06) * mm});
            skLineSegment(sketch, "E178.MirrorCS", {"start": v(60.4, 43.39) * mm, "end": v(61.3, 43.9) * mm});
            skLineSegment(sketch, "E179", {"start": v(29.77, 49.45) * mm, "end": v(37.5, 62.85) * mm});
            skLineSegment(sketch, "E180", {"start": v(37.5, 62.85) * mm, "end": v(45.23, 49.45) * mm});
            skLineSegment(sketch, "E181", {"start": v(33.63, 56.15) * mm, "end": v(33.63, 36.05) * mm});
            skLineSegment(sketch, "E182", {"start": v(33.63, 36.05) * mm, "end": v(30.38, 36.05) * mm});
            skLineSegment(sketch, "E183", {"start": v(30.38, 36.05) * mm, "end": v(30.38, 50.5) * mm});
            skLineSegment(sketch, "E184", {"start": v(33.63, 44.98) * mm, "end": v(37.5, 44.98) * mm});
            skLineSegment(sketch, "E185", {"start": v(33.63, 36.05) * mm, "end": v(33.63, 44.98) * mm});
            skLineSegment(sketch, "E186", {"start": v(33.63, 40.52) * mm, "end": v(33.63, 44.98) * mm});
            skLineSegment(sketch, "E187", {"start": v(33.63, 42.75) * mm, "end": v(33.63, 44.98) * mm});
            skLineSegment(sketch, "E188", {"start": v(33.63, 43.87) * mm, "end": v(37.5, 43.87) * mm});
            skLineSegment(sketch, "E189", {"start": v(44.62, 50.5) * mm, "end": v(44.62, 36.05) * mm});
            skLineSegment(sketch, "E190", {"start": v(41.37, 56.15) * mm, "end": v(41.37, 36.05) * mm});
            skLineSegment(sketch, "E191", {"start": v(37.4, 44.98) * mm, "end": v(33.63, 44.98) * mm});
            skLineSegment(sketch, "E192", {"start": v(37.5, 43.87) * mm, "end": v(41.37, 43.87) * mm});
            skLineSegment(sketch, "E193", {"start": v(37.5, 44.98) * mm, "end": v(41.37, 44.98) * mm});
            skLineSegment(sketch, "E194", {"start": v(41.37, 36.05) * mm, "end": v(41.37, 44.98) * mm});
            skLineSegment(sketch, "E195", {"start": v(41.37, 36.05) * mm, "end": v(41.37, 43.87) * mm});
            skLineSegment(sketch, "E196", {"start": v(41.37, 44.98) * mm, "end": v(41.37, 43.87) * mm});
            skLineSegment(sketch, "E197.MirrorCS", {"start": v(37.5, 46.1) * mm, "end": v(41.37, 46.1) * mm});
            skLineSegment(sketch, "E198.MirrorCS", {"start": v(33.63, 46.1) * mm, "end": v(37.5, 46.1) * mm});
            skLineSegment(sketch, "E199", {"start": v(37.5, 44.98) * mm, "end": v(37.5, 79.98) * mm});
            skSolve(sketch);
        }
        {
            var Q0;
            {var subQ0=sQuery(id+"F11.wireOp",EDGE,"E158");Q0=makeQuery(id+"F11.imprint","IMPRINT",FACE,{"disambiguationData":[TD([[makeQuery(id+"F11.imprint","IMPRINT",EDGE,{"derivedFrom":subQ0}),1.0]])]});}
            var Q1;
            {var subQ3=sQuery(id+"F11.wireOp",EDGE,"E185");Q1=makeQuery(id+"F11.imprint","IMPRINT",FACE,{"disambiguationData":[TD([[makeQuery(id+"F11.imprint","IMPRINT",EDGE,{"derivedFrom":subQ3}),-1.0]])]});}
            var Q2;
            {var subQ5=sQuery(id+"F11.wireOp",EDGE,"E197.MirrorCS");Q2=makeQuery(id+"F11.imprint","IMPRINT",FACE,{"disambiguationData":[TD([[makeQuery(id+"F11.imprint","IMPRINT",EDGE,{"derivedFrom":subQ5}),1.0]])]});}
            var Q3;
            {var subQ5=sQuery(id+"F11.wireOp",EDGE,"E198.MirrorCS");Q3=makeQuery(id+"F11.imprint","IMPRINT",FACE,{"disambiguationData":[TD([[makeQuery(id+"F11.imprint","IMPRINT",EDGE,{"derivedFrom":subQ5}),1.0]])]});}
            var Q4;
            {var subQ0=sQuery(id+"F11.wireOp",EDGE,"E159");Q4=makeQuery(id+"F11.imprint","IMPRINT",FACE,{"disambiguationData":[TD([[makeQuery(id+"F11.imprint","IMPRINT",EDGE,{"derivedFrom":subQ0}),1.0]])]});}
            var Q5;
            {var subQ3=sQuery(id+"F11.wireOp",EDGE,"E152.MirrorCS");Q5=makeQuery(id+"F11.imprint","IMPRINT",FACE,{"disambiguationData":[TD([[makeQuery(id+"F11.imprint","IMPRINT",EDGE,{"derivedFrom":subQ3}),1.0]])]});}
            var Q6;
            {var subQ3=sQuery(id+"F11.wireOp",EDGE,"E152.MirrorCS");Q6=makeQuery(id+"F11.imprint","IMPRINT",FACE,{"disambiguationData":[TD([[makeQuery(id+"F11.imprint","IMPRINT",EDGE,{"derivedFrom":subQ3}),-1.0]])]});}
            var Q7;
            {var subQ3=sQuery(id+"F11.wireOp",EDGE,"E154.MirrorCS");Q7=makeQuery(id+"F11.imprint","IMPRINT",FACE,{"disambiguationData":[TD([[makeQuery(id+"F11.imprint","IMPRINT",EDGE,{"derivedFrom":subQ3}),1.0]])]});}
            var Q8;
            {var subQ3=sQuery(id+"F11.wireOp",EDGE,"E148");Q8=makeQuery(id+"F11.imprint","IMPRINT",FACE,{"disambiguationData":[TD([[makeQuery(id+"F11.imprint","IMPRINT",EDGE,{"derivedFrom":subQ3}),1.0]])]});}
            var Q9;
            Q9=makeQuery(id+"F11.imprint","IMPRINT",FACE,{"disambiguationData":[TD([[makeQuery(id+"F11.imprint","IMPRINT",EDGE,{"derivedFrom":sQuery(id+"F11.wireOp",EDGE,"E147")}),-1.0]])]});
            var Q10;
            {var subQ3=sQuery(id+"F11.wireOp",EDGE,"E151.MirrorCS");Q10=makeQuery(id+"F11.imprint","IMPRINT",FACE,{"disambiguationData":[TD([[makeQuery(id+"F11.imprint","IMPRINT",EDGE,{"derivedFrom":subQ3}),1.0]])]});}
            var Q11;
            {var subQ2=sQuery(id+"F11.wireOp",EDGE,"E153.MirrorCS");Q11=makeQuery(id+"F11.imprint","IMPRINT",FACE,{"disambiguationData":[TD([[makeQuery(id+"F11.imprint","IMPRINT",EDGE,{"derivedFrom":subQ2}),1.0]])]});}
            var Q12;
            {var subQ3=sQuery(id+"F11.wireOp",EDGE,"E156.MirrorCS");Q12=makeQuery(id+"F11.imprint","IMPRINT",FACE,{"disambiguationData":[TD([[makeQuery(id+"F11.imprint","IMPRINT",EDGE,{"derivedFrom":subQ3}),-1.0]])]});}
            var Q13;
            {var subQ3=sQuery(id+"F11.wireOp",EDGE,"E153.MirrorCS");Q13=makeQuery(id+"F11.imprint","IMPRINT",FACE,{"disambiguationData":[TD([[makeQuery(id+"F11.imprint","IMPRINT",EDGE,{"derivedFrom":subQ3}),-1.0]])]});}
            var Q14;
            {var subQ0=sQuery(id+"F11.wireOp",EDGE,"E129.MirrorCS");Q14=makeQuery(id+"F11.imprint","IMPRINT",FACE,{"disambiguationData":[TD([[makeQuery(id+"F11.imprint","IMPRINT",EDGE,{"derivedFrom":subQ0}),1.0]])]});}
            var Q15;
            {var subQ0=sQuery(id+"F11.wireOp",EDGE,"E136.MirrorCS");Q15=makeQuery(id+"F11.imprint","IMPRINT",FACE,{"disambiguationData":[TD([[makeQuery(id+"F11.imprint","IMPRINT",EDGE,{"derivedFrom":subQ0}),1.0]])]});}
            var Q16;
            {var subQ0=sQuery(id+"F11.wireOp",EDGE,"E135.MirrorCS");Q16=makeQuery(id+"F11.imprint","IMPRINT",FACE,{"disambiguationData":[TD([[makeQuery(id+"F11.imprint","IMPRINT",EDGE,{"derivedFrom":subQ0}),-1.0]])]});}
            var Q17;
            {var subQ0=sQuery(id+"F11.wireOp",EDGE,"E133");Q17=makeQuery(id+"F11.imprint","IMPRINT",FACE,{"disambiguationData":[TD([[makeQuery(id+"F11.imprint","IMPRINT",EDGE,{"derivedFrom":subQ0}),1.0]])]});}
            var Q18;
            {var subQ0=sQuery(id+"F11.wireOp",EDGE,"E122");Q18=makeQuery(id+"F11.imprint","IMPRINT",FACE,{"disambiguationData":[TD([[makeQuery(id+"F11.imprint","IMPRINT",EDGE,{"derivedFrom":subQ0}),-1.0]])]});}
            var Q19;
            {var subQ0=sQuery(id+"F11.wireOp",EDGE,"E122");Q19=makeQuery(id+"F11.imprint","IMPRINT",FACE,{"disambiguationData":[TD([[makeQuery(id+"F11.imprint","IMPRINT",EDGE,{"derivedFrom":subQ0}),1.0]])]});}
            var Q20;
            {var subQ0=sQuery(id+"F11.wireOp",EDGE,"E126.MirrorCS");Q20=makeQuery(id+"F11.imprint","IMPRINT",FACE,{"disambiguationData":[TD([[makeQuery(id+"F11.imprint","IMPRINT",EDGE,{"derivedFrom":subQ0}),-1.0]])]});}
            var Q21;
            {var subQ5=sQuery(id+"F11.wireOp",EDGE,"E126.MirrorCS");Q21=makeQuery(id+"F11.imprint","IMPRINT",FACE,{"disambiguationData":[TD([[makeQuery(id+"F11.imprint","IMPRINT",EDGE,{"derivedFrom":subQ5}),1.0]])]});}
            var Q22;
            {var subQ0=sQuery(id+"F11.wireOp",EDGE,"E127.MirrorCS");Q22=makeQuery(id+"F11.imprint","IMPRINT",FACE,{"disambiguationData":[TD([[makeQuery(id+"F11.imprint","IMPRINT",EDGE,{"derivedFrom":subQ0}),1.0]])]});}
            var Q23;
            {var subQ0=sQuery(id+"F11.wireOp",EDGE,"E123");Q23=makeQuery(id+"F11.imprint","IMPRINT",FACE,{"disambiguationData":[TD([[makeQuery(id+"F11.imprint","IMPRINT",EDGE,{"derivedFrom":subQ0}),1.0]])]});}
            var Q24;
            {var subQ0=sQuery(id+"F11.wireOp",EDGE,"E123");Q24=makeQuery(id+"F11.imprint","IMPRINT",FACE,{"disambiguationData":[TD([[makeQuery(id+"F11.imprint","IMPRINT",EDGE,{"derivedFrom":subQ0}),-1.0]])]});}
            var Q25;
            {var subQ0=sQuery(id+"F11.wireOp",EDGE,"E134");Q25=makeQuery(id+"F11.imprint","IMPRINT",FACE,{"disambiguationData":[TD([[makeQuery(id+"F11.imprint","IMPRINT",EDGE,{"derivedFrom":subQ0}),1.0]])]});}
            var Q26;
            {var subQ0=sQuery(id+"F11.wireOp",EDGE,"E138.MirrorCS");Q26=makeQuery(id+"F11.imprint","IMPRINT",FACE,{"disambiguationData":[TD([[makeQuery(id+"F11.imprint","IMPRINT",EDGE,{"derivedFrom":subQ0}),1.0]])]});}
            var Q27;
            {var subQ0=sQuery(id+"F11.wireOp",EDGE,"E137.MirrorCS");Q27=makeQuery(id+"F11.imprint","IMPRINT",FACE,{"disambiguationData":[TD([[makeQuery(id+"F11.imprint","IMPRINT",EDGE,{"derivedFrom":subQ0}),-1.0]])]});}
            var Q28;
            {var subQ0=sQuery(id+"F11.wireOp",EDGE,"E132.MirrorCS");Q28=makeQuery(id+"F11.imprint","IMPRINT",FACE,{"disambiguationData":[TD([[makeQuery(id+"F11.imprint","IMPRINT",EDGE,{"derivedFrom":subQ0}),-1.0]])]});}
            var Q29;
            {var subQ0=sQuery(id+"F11.wireOp",EDGE,"E132.MirrorCS");Q29=makeQuery(id+"F11.imprint","IMPRINT",FACE,{"disambiguationData":[TD([[makeQuery(id+"F11.imprint","IMPRINT",EDGE,{"derivedFrom":subQ0}),1.0]])]});}
            var Q30;
            {var subQ0=sQuery(id+"F11.wireOp",EDGE,"E131.MirrorCS");Q30=makeQuery(id+"F11.imprint","IMPRINT",FACE,{"disambiguationData":[TD([[makeQuery(id+"F11.imprint","IMPRINT",EDGE,{"derivedFrom":subQ0}),-1.0]])]});}
            var Q31;
            {var subQ0=sQuery(id+"F11.wireOp",EDGE,"E131.MirrorCS");Q31=makeQuery(id+"F11.imprint","IMPRINT",FACE,{"disambiguationData":[TD([[makeQuery(id+"F11.imprint","IMPRINT",EDGE,{"derivedFrom":subQ0}),1.0]])]});}
            var Q32;
            {var subQ0=sQuery(id+"F11.wireOp",EDGE,"E130.MirrorCS");Q32=makeQuery(id+"F11.imprint","IMPRINT",FACE,{"disambiguationData":[TD([[makeQuery(id+"F11.imprint","IMPRINT",EDGE,{"derivedFrom":subQ0}),-1.0]])]});}
            var Q33;
            {var subQ0=sQuery(id+"F11.wireOp",EDGE,"E129.MirrorCS");Q33=makeQuery(id+"F11.imprint","IMPRINT",FACE,{"disambiguationData":[TD([[makeQuery(id+"F11.imprint","IMPRINT",EDGE,{"derivedFrom":subQ0}),-1.0]])]});}
            var Q34;
            {var subQ0=sQuery(id+"F11.wireOp",EDGE,"E130.MirrorCS");Q34=makeQuery(id+"F11.imprint","IMPRINT",FACE,{"disambiguationData":[TD([[makeQuery(id+"F11.imprint","IMPRINT",EDGE,{"derivedFrom":subQ0}),1.0]])]});}
            extrude(context, id + "F12", {"entities" : qUnion([Q0, Q1, Q2, Q3, Q4, Q5, Q6, Q7, Q8, Q9, Q10, Q11, Q12, Q13, Q14, Q15, Q16, Q17, Q18, Q19, Q20, Q21, Q22, Q23, Q24, Q25, Q26, Q27, Q28, Q29, Q30, Q31, Q32, Q33, Q34]), "operationType" : NewBodyOperationType.REMOVE, "oppositeDirection" : true, "depth" : 2 * mm, "offsetDistance" : 25 * mm});
        }
        {
            var Q0;
            Q0=makeQuery(id+"F1.opExtrude","SWEPT_FACE",FACE,{"disambiguationData":[OSD([sQuery(id+"F0.wireOp",EDGE,"E0.top"),sQuery(id+"F0.wireOp",EDGE,"E3")])]});
            var sketch = newSketch(context, id + "F13", { "sketchPlane" : qUnion([Q0])});
            skLineSegment(sketch, "E200", {"start": v(0, 0) * mm, "end": v(0, -37.5) * mm});
            skPoint(sketch, "E200.endSnap0", {"position": v(-31.5, -37.5) * mm});
            skCircle(sketch, "E201", {"center": v(0, -37.5) * mm, "radius": 15 * mm});
            skSolve(sketch);
        }
        {
            var Q0;
            Q0 = qSketchRegion(id + "F13", true);
            extrude(context, id + "F14", {"entities" : qUnion([Q0]), "operationType" : NewBodyOperationType.REMOVE, "oppositeDirection" : true, "depth" : 25 * mm, "offsetDistance" : 25 * mm});
        }
    });
